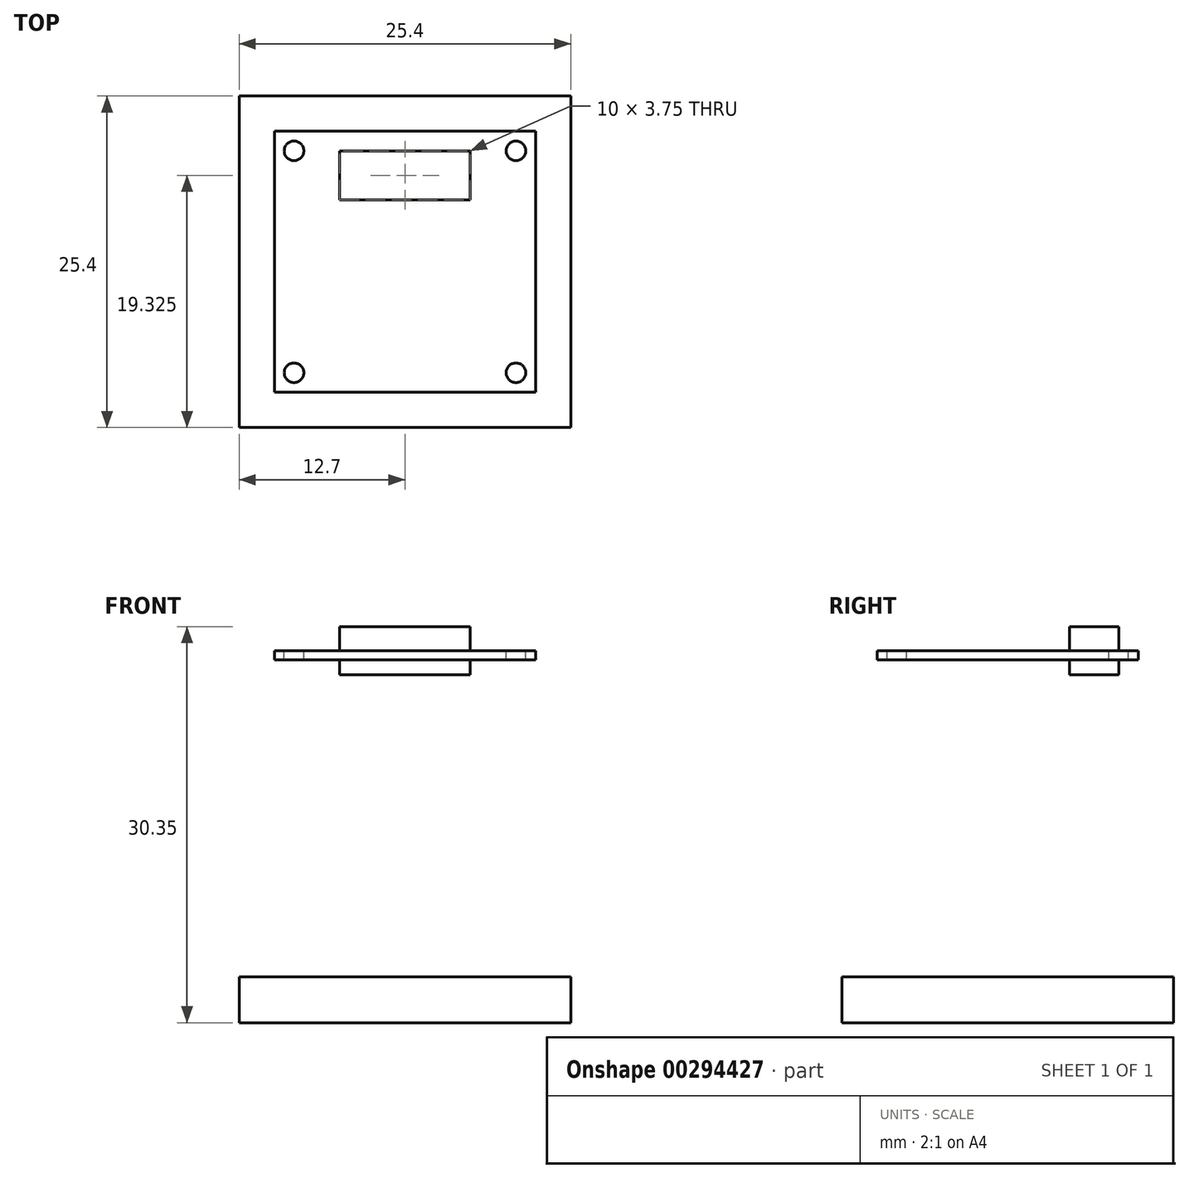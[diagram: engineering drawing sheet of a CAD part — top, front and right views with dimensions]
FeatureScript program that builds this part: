
annotation { "Feature Type Name" : "Feature", "Feature Type Description" : "" }
export const myFeature = defineFeature(function(context is Context, id is Id, definition is map)
    precondition{}
    {
        {
            var Q0;
            Q0=qCreatedBy(makeId("Top.planeOp"),FACE);
            var sketch = newSketch(context, id + "F0", { "sketchPlane" : qUnion([Q0])});
            skLineSegment(sketch, "E0.bottom", {"start": v(-10, 10) * mm, "end": v(10, 10) * mm});
            skLineSegment(sketch, "E0.top", {"start": v(-10, -10) * mm, "end": v(10, -10) * mm});
            skLineSegment(sketch, "E0.left", {"start": v(-10, 10) * mm, "end": v(-10, -10) * mm});
            skLineSegment(sketch, "E0.right", {"start": v(10, 10) * mm, "end": v(10, -10) * mm});
            skPoint(sketch, "E0.middle", {"position": v(0, 0) * mm});
            skLineSegment(sketch, "E1.bottom", {"start": v(-8.5, 8.5) * mm, "end": v(8.5, 8.5) * mm, "construction": true});
            skLineSegment(sketch, "E1.top", {"start": v(-8.5, -8.5) * mm, "end": v(8.5, -8.5) * mm, "construction": true});
            skLineSegment(sketch, "E1.left", {"start": v(-8.5, 8.5) * mm, "end": v(-8.5, -8.5) * mm, "construction": true});
            skLineSegment(sketch, "E1.right", {"start": v(8.5, 8.5) * mm, "end": v(8.5, -8.5) * mm, "construction": true});
            skLineSegment(sketch, "E2.bottom", {"start": v(-5, 8.5) * mm, "end": v(5, 8.5) * mm});
            skLineSegment(sketch, "E2.top", {"start": v(-5, 4.75) * mm, "end": v(5, 4.75) * mm});
            skLineSegment(sketch, "E2.left", {"start": v(-5, 8.5) * mm, "end": v(-5, 4.75) * mm});
            skLineSegment(sketch, "E2.right", {"start": v(5, 8.5) * mm, "end": v(5, 4.75) * mm});
            skPoint(sketch, "E3", {"position": v(0, 4.75) * mm});
            skSolve(sketch);
        }
        {
            var Q0;
            Q0 = qSketchRegion(id + "F0", true);
            var Q1;
            Q1=makeQuery(id+"F0.imprint","IMPRINT",FACE,{"disambiguationData":[TD([[makeQuery(id+"F0.imprint","IMPRINT",EDGE,{"derivedFrom":sQuery(id+"F0.wireOp",EDGE,"E2.bottom")}),-1.0]])]});
            extrude(context, id + "F1", {"entities" : qUnion([Q0, Q1]), "oppositeDirection" : true, "depth" : .7 * mm});
        }
        {
            var Q0;
            Q0=sQuery(id+"F0.wireOp",VERTEX,"E1.left.start");
            var Q1;
            Q1=sQuery(id+"F0.wireOp",VERTEX,"E1.bottom.end");
            var Q2;
            Q2=sQuery(id+"F0.wireOp",VERTEX,"E1.right.end");
            var Q3;
            Q3=sQuery(id+"F0.wireOp",VERTEX,"E1.left.end");
            var Q4;
            Q4=makeQuery(id+"F1.opExtrude","SWEPT_BODY",BODY,{"disambiguationData":[OSD([sQuery(id+"F0.wireOp",EDGE,"E0.bottom"),sQuery(id+"F0.wireOp",EDGE,"E0.top"),sQuery(id+"F0.wireOp",EDGE,"E0.left"),sQuery(id+"F0.wireOp",EDGE,"E0.right")])]});
            hole(context, id + "F2", {"style" : HoleStyle.SIMPLE, "endStyle" : HoleEndStyle.THROUGH, "holeDiameter" : 1.5 * mm, "tappedDepth" : 12.7 * mm, "tapClearance" : 3, "locations" : qUnion([Q0, Q1, Q2, Q3]), "scope" : qUnion([Q4])});
        }
        {
            var Q0;
            Q0=qCreatedBy(makeId("Top.planeOp"),FACE);
            var sketch = newSketch(context, id + "F3", { "sketchPlane" : qUnion([Q0])});
            skLineSegment(sketch, "E4.0", {"start": v(-5, 8.5) * mm, "end": v(5, 8.5) * mm});
            skLineSegment(sketch, "E4.1", {"start": v(5, 8.5) * mm, "end": v(5, 4.75) * mm});
            skLineSegment(sketch, "E4.2", {"start": v(-5, 4.75) * mm, "end": v(5, 4.75) * mm});
            skLineSegment(sketch, "E4.3", {"start": v(-5, 8.5) * mm, "end": v(-5, 4.75) * mm});
            skSolve(sketch);
        }
        {
            var Q0;
            Q0 = qSketchRegion(id + "F3", true);
            extrude(context, id + "F4", {"entities" : qUnion([Q0]), "operationType" : NewBodyOperationType.ADD, "endBound" : BoundingType.SYMMETRIC, "depth" : 3.7 * mm});
        }
        {
            var Q0;
            Q0=qCreatedBy(makeId("Top.planeOp"),FACE);
            cPlane(context, id + "F5", {"entities" : qUnion([Q0]), "cplaneType" : CPlaneType.OFFSET, "offset" : 25 * mm, "oppositeDirection" : true, "width" : 150 * mm, "height" : 150 * mm});
        }
        {
            var Q0;
            Q0=qCreatedBy(id+"F5.planeOp",FACE);
            var sketch = newSketch(context, id + "F6", { "sketchPlane" : qUnion([Q0])});
            skLineSegment(sketch, "E5.bottom", {"start": v(-12.7, -12.7) * mm, "end": v(12.7, -12.7) * mm});
            skLineSegment(sketch, "E5.top", {"start": v(-12.7, 12.7) * mm, "end": v(12.7, 12.7) * mm});
            skLineSegment(sketch, "E5.left", {"start": v(-12.7, -12.7) * mm, "end": v(-12.7, 12.7) * mm});
            skLineSegment(sketch, "E5.right", {"start": v(12.7, -12.7) * mm, "end": v(12.7, 12.7) * mm});
            skPoint(sketch, "E5.middle", {"position": v(0, 0) * mm});
            skSolve(sketch);
        }
        {
            var Q0;
            Q0=makeQuery(id+"F6.imprint","IMPRINT",FACE,{"disambiguationData":[TD([[makeQuery(id+"F6.imprint","IMPRINT",EDGE,{"derivedFrom":sQuery(id+"F6.wireOp",EDGE,"E5.bottom")}),1.0]])]});
            extrude(context, id + "F7", {"entities" : qUnion([Q0]), "oppositeDirection" : true, "depth" : 3.5 * mm});
        }
    });
